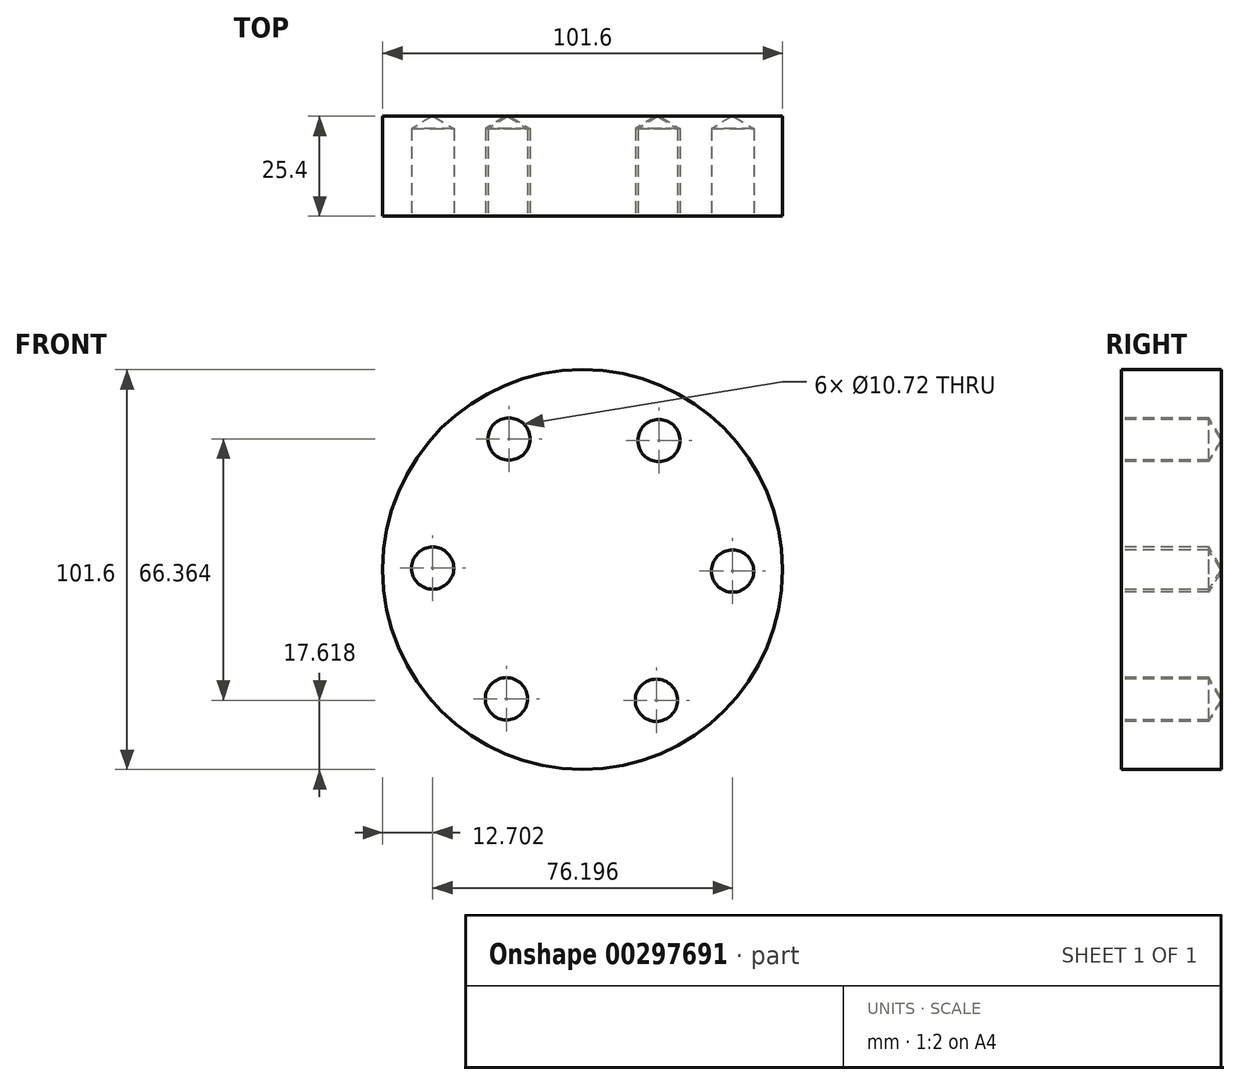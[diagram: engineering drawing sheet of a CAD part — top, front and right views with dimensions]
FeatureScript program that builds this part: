
annotation { "Feature Type Name" : "Feature", "Feature Type Description" : "" }
export const myFeature = defineFeature(function(context is Context, id is Id, definition is map)
    precondition{}
    {
        {
            var Q0;
            Q0=qCreatedBy(makeId("Front.planeOp"),FACE);
            var sketch = newSketch(context, id + "F0", { "sketchPlane" : qUnion([Q0])});
            skCircle(sketch, "E0", {"center": v(0, 0) * mm, "radius": 50.8 * mm});
            skSolve(sketch);
        }
        {
            var Q0;
            Q0 = qSketchRegion(id + "F0", true);
            extrude(context, id + "F1", {"entities" : qUnion([Q0]), "depth" : 25.4 * mm});
        }
        {
            var Q0;
            Q0=makeQuery(id+"F1.opExtrude","CAP_FACE",FACE,{"disambiguationData":[OSD([sQuery(id+"F0.wireOp",EDGE,"E0")])],"isStart":false});
            var sketch = newSketch(context, id + "F2", { "sketchPlane" : qUnion([Q0])});
            skCircle(sketch, "E1.cCircle", {"center": v(0, 0) * mm, "radius": 33 * mm, "construction": true});
            skLineSegment(sketch, "E1.0", {"start": v(38.1, -0.38) * mm, "end": v(18.72, -33.18) * mm, "construction": true});
            skLineSegment(sketch, "E1.1", {"start": v(18.72, -33.18) * mm, "end": v(-19.37, -32.8) * mm, "construction": true});
            skLineSegment(sketch, "E1.2", {"start": v(-19.37, -32.8) * mm, "end": v(-38.1, 0.38) * mm, "construction": true});
            skLineSegment(sketch, "E1.3", {"start": v(-38.1, 0.38) * mm, "end": v(-18.72, 33.18) * mm, "construction": true});
            skLineSegment(sketch, "E1.4", {"start": v(-18.72, 33.18) * mm, "end": v(19.37, 32.8) * mm, "construction": true});
            skLineSegment(sketch, "E1.5", {"start": v(19.37, 32.8) * mm, "end": v(38.1, -0.38) * mm, "construction": true});
            skPoint(sketch, "E1.0.midPoint", {"position": v(28.41, -16.78) * mm});
            skPoint(sketch, "E2", {"position": v(-18.72, 33.18) * mm});
            skPoint(sketch, "E3", {"position": v(-38.1, 0.38) * mm});
            skPoint(sketch, "E4", {"position": v(-19.37, -32.8) * mm});
            skPoint(sketch, "E5", {"position": v(18.72, -33.18) * mm});
            skPoint(sketch, "E6", {"position": v(38.1, -0.38) * mm});
            skPoint(sketch, "E7", {"position": v(19.37, 32.8) * mm});
            skSolve(sketch);
        }
        {
            var Q0;
            Q0=sQuery(id+"F2.wireOp",VERTEX,"E3");
            var Q1;
            Q1=sQuery(id+"F2.wireOp",VERTEX,"E2");
            var Q2;
            Q2=sQuery(id+"F2.wireOp",VERTEX,"E7");
            var Q3;
            Q3=sQuery(id+"F2.wireOp",VERTEX,"E6");
            var Q4;
            Q4=sQuery(id+"F2.wireOp",VERTEX,"E5");
            var Q5;
            Q5=sQuery(id+"F2.wireOp",VERTEX,"E4");
            var Q6;
            Q6=makeQuery(id+"F1.opExtrude","SWEPT_BODY",BODY,{"disambiguationData":[OSD([sQuery(id+"F0.wireOp",EDGE,"E0")])]});
            hole(context, id + "F3", {"style" : HoleStyle.SIMPLE, "endStyle" : HoleEndStyle.BLIND, "standardTappedOrClearance" : lookupTablePath({ "standard" : "ANSI", "engagement" : "75%", "pitch" : "13 tpi", "size" : "1/2", "type" : "Tapped" }), "standardBlindInLast" : lookupTablePath({ "standard" : "ANSI", "engagement" : "75%", "pitch" : "13 tpi", "size" : "1/2", "type" : "Tapped" }), "holeDiameter" : 10.72 * mm, "showTappedDepth" : true, "holeDepth" : 22.22 * mm, "tappedDepth" : 18.32 * mm, "tapClearance" : 2, "startFromSketch" : true, "locations" : qUnion([Q0, Q1, Q2, Q3, Q4, Q5]), "scope" : qUnion([Q6]), "majorDiameter" : 12.7 * mm});
        }
    });
